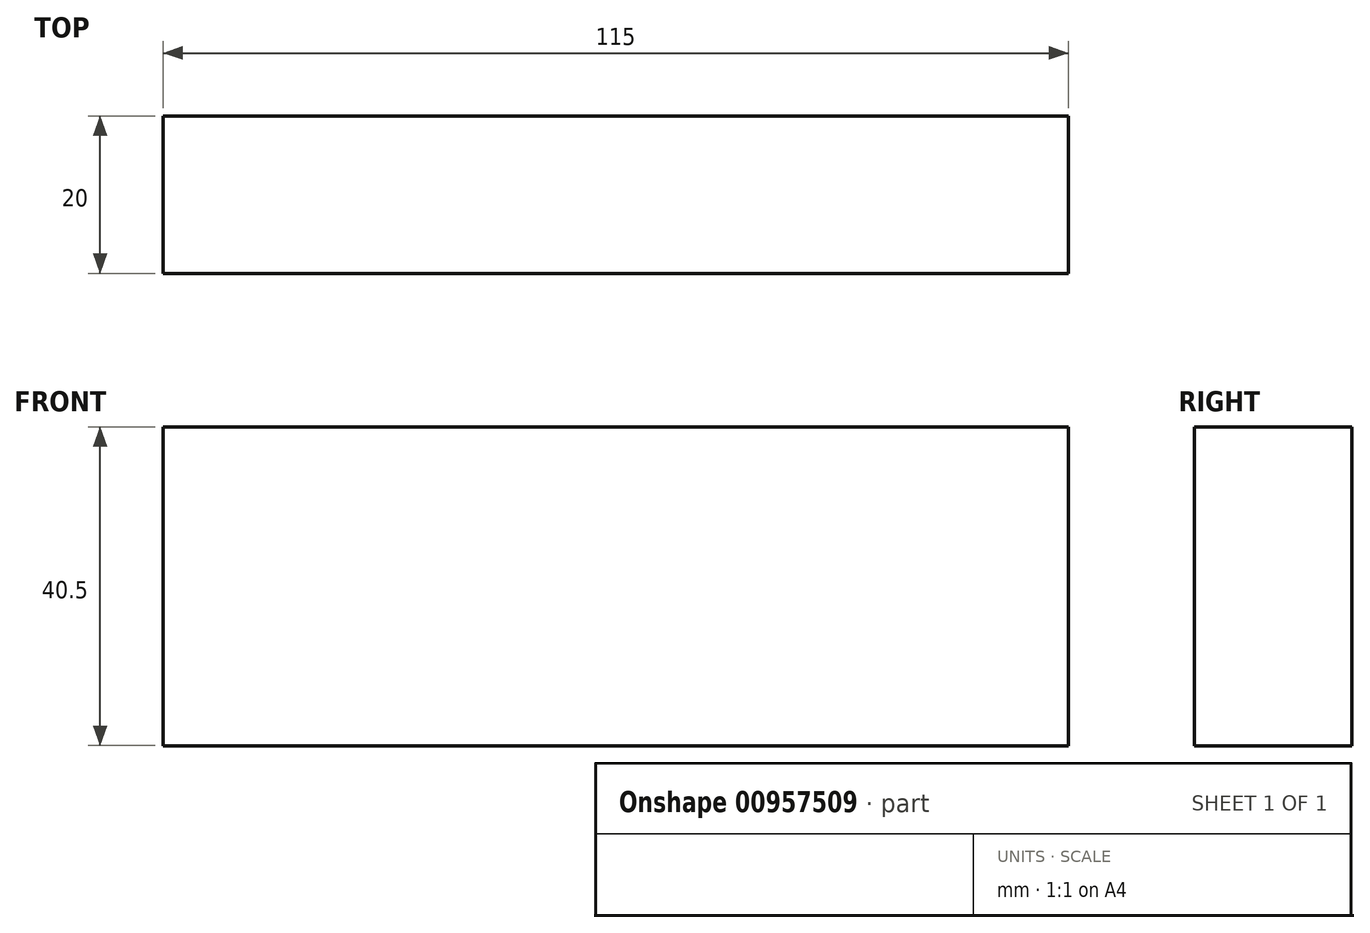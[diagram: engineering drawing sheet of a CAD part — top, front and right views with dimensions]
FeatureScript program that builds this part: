
annotation { "Feature Type Name" : "Feature", "Feature Type Description" : "" }
export const myFeature = defineFeature(function(context is Context, id is Id, definition is map)
    precondition{}
    {
        {
            var Q0;
            Q0=qCreatedBy(makeId("Front.planeOp"),FACE);
            var sketch = newSketch(context, id + "F0", { "sketchPlane" : qUnion([Q0])});
            skLineSegment(sketch, "E0.bottom", {"start": v(-83.64, 7.5) * mm, "end": v(31.36, 7.5) * mm});
            skLineSegment(sketch, "E0.top", {"start": v(-83.64, -33) * mm, "end": v(31.36, -33) * mm});
            skLineSegment(sketch, "E0.left", {"start": v(-83.64, 7.5) * mm, "end": v(-83.64, -33) * mm});
            skLineSegment(sketch, "E0.right", {"start": v(31.36, 7.5) * mm, "end": v(31.36, -33) * mm});
            skSolve(sketch);
        }
        {
            var Q0;
            Q0 = qSketchRegion(id + "F0", true);
            extrude(context, id + "F1", {"entities" : qUnion([Q0]), "depth" : 20 * mm, "offsetDistance" : 25 * mm});
        }
    });
